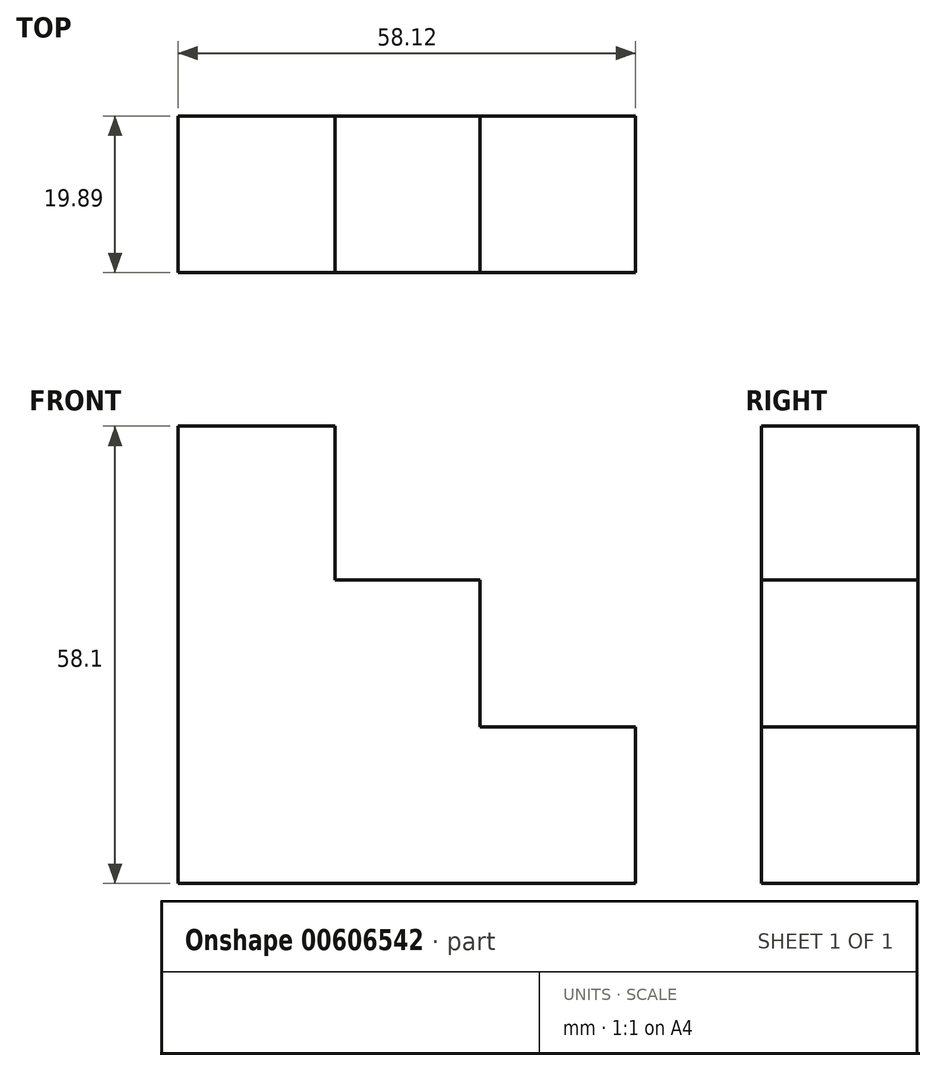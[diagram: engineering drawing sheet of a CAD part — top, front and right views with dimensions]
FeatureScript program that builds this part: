
annotation { "Feature Type Name" : "Feature", "Feature Type Description" : "" }
export const myFeature = defineFeature(function(context is Context, id is Id, definition is map)
    precondition{}
    {
        {
            var Q0;
            Q0=qCreatedBy(makeId("Front.planeOp"),FACE);
            var sketch = newSketch(context, id + "F0", { "sketchPlane" : qUnion([Q0])});
            skLineSegment(sketch, "E0", {"start": v(0, 0) * mm, "end": v(58.12, 0) * mm});
            skLineSegment(sketch, "E1", {"start": v(58.12, 0) * mm, "end": v(58.12, 19.9) * mm});
            skLineSegment(sketch, "E2", {"start": v(58.12, 19.9) * mm, "end": v(38.34, 19.9) * mm});
            skLineSegment(sketch, "E3", {"start": v(38.34, 19.9) * mm, "end": v(38.34, 38.55) * mm});
            skLineSegment(sketch, "E4", {"start": v(38.34, 38.55) * mm, "end": v(19.94, 38.55) * mm});
            skLineSegment(sketch, "E5", {"start": v(19.94, 38.55) * mm, "end": v(19.94, 58.1) * mm});
            skLineSegment(sketch, "E6", {"start": v(19.94, 58.1) * mm, "end": v(0, 58.1) * mm});
            skLineSegment(sketch, "E7", {"start": v(0, 58.1) * mm, "end": v(0, 0) * mm});
            skSolve(sketch);
        }
        {
            var Q0;
            Q0 = qSketchRegion(id + "F0", true);
            extrude(context, id + "F1", {"entities" : qUnion([Q0]), "depth" : 19.9 * mm, "offsetDistance" : 25.4 * mm});
        }
    });
